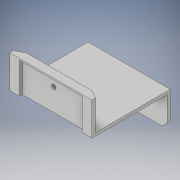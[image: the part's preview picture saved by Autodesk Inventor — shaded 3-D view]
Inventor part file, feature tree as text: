
AUTODESK INVENTOR PART (.ipt)
format: ipt  version: 2019 (Build 230136000, 136)  size: 160,768 bytes
history: native  units: mm
features: extrude x4, sketch x2, plane x2, split x2, draft x1, direct_edit x1, chamfer x1, projected_geometry x1, move_body x1
ambient origin geometry x8: Origin, YZ Plane, XZ Plane, XY Plane, X Axis, Y Axis, Z Axis, Center Point
bodies: Solid1 (feature_tree)
feature tree (15):
  sketch  "Sketch1"  dims[d0=3.0mm d1=7.0mm]
  extrude  "Extrusion1"  Depth=7.0mm
  extrude  "Extrusion2"  Depth=20.0mm
  extrude  "Extrusion3"  Depth=2.0mm
  draft  "FaceDraft1"
  extrude  "Extrusion4"  Depth=1.0mm
  direct_edit  "Direct Edit1"
  plane  "Work Plane1"
  plane  "Work Plane2"
  split  "Split1"
  split  "Split2"
  chamfer  "Chamfer1"  Distance=1.0mm
  sketch  "Sketch2"  dims[d2=44.0mm d3=20.0mm d4=15.0mm d5=1.0mm d8=1.0mm d9=1.0mm d10=55.0mm d11=5.5mm d12=0.0mm d13=3.5mm d14=0.0mm d15=3.5mm d16=47.0mm d17=0.0mm d18=0.0mm d19=60.0deg d20=2.0mm d21=20.0mm d22=0.0mm d23=0.0mm d24=0.0mm d25=2.0mm d26=0.0mm d27=0.0mm d28=3.5mm d29=2.0mm d30=45.0deg]
  projected_geometry  "Projected Loop1"
  move_body  "Move1"
